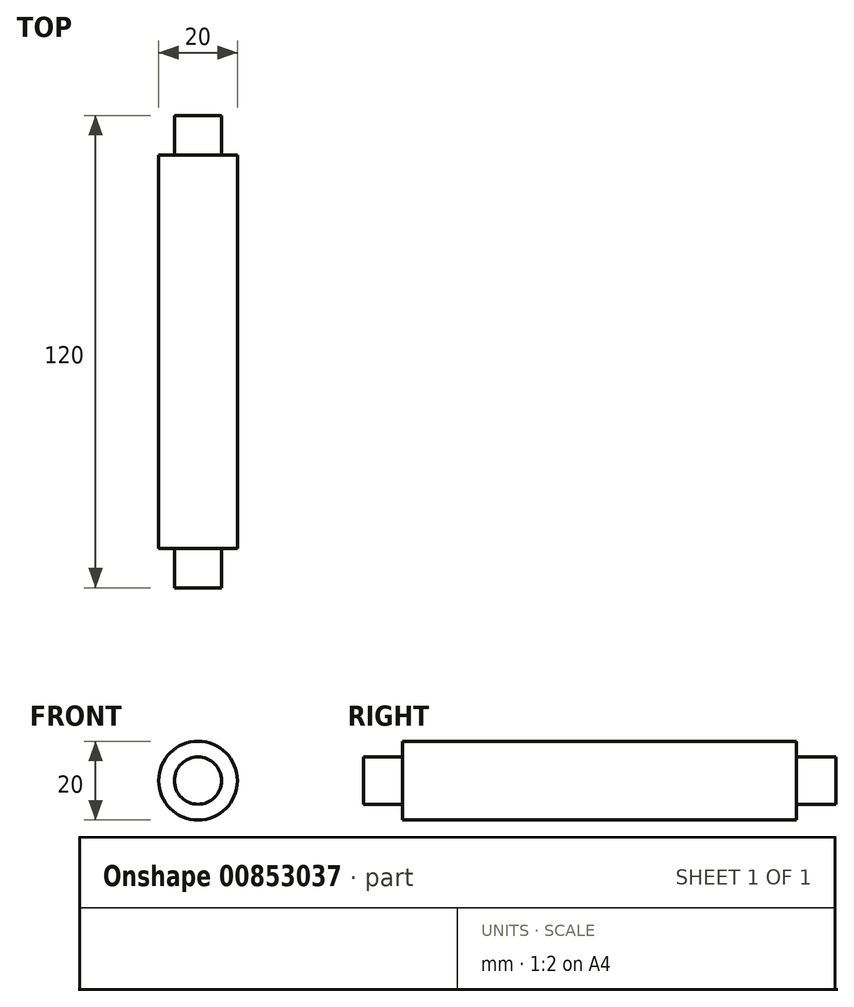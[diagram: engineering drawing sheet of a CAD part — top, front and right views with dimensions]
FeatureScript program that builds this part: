
annotation { "Feature Type Name" : "Feature", "Feature Type Description" : "" }
export const myFeature = defineFeature(function(context is Context, id is Id, definition is map)
    precondition{}
    {
        {
            var Q0;
            Q0=qCreatedBy(makeId("Top.planeOp"),FACE);
            var sketch = newSketch(context, id + "F0", { "sketchPlane" : qUnion([Q0])});
            skLineSegment(sketch, "E0.bottom", {"start": v(5.8, 50) * mm, "end": v(9.8, 50) * mm});
            skLineSegment(sketch, "E0.top", {"start": v(5.8, -50) * mm, "end": v(9.8, -50) * mm});
            skLineSegment(sketch, "E0.left", {"start": v(-0.2, 50) * mm, "end": v(-0.2, -50) * mm});
            skLineSegment(sketch, "E0.right", {"start": v(9.8, 50) * mm, "end": v(9.8, -50) * mm});
            skLineSegment(sketch, "E1.top", {"start": v(-0.2, 60) * mm, "end": v(5.8, 60) * mm});
            skLineSegment(sketch, "E1.left", {"start": v(-0.2, 50) * mm, "end": v(-0.2, 60) * mm});
            skLineSegment(sketch, "E1.right", {"start": v(5.8, 50) * mm, "end": v(5.8, 60) * mm});
            skLineSegment(sketch, "E2.top", {"start": v(-0.2, -60) * mm, "end": v(5.8, -60) * mm});
            skLineSegment(sketch, "E2.left", {"start": v(-0.2, -50) * mm, "end": v(-0.2, -60) * mm});
            skLineSegment(sketch, "E2.right", {"start": v(5.8, -50) * mm, "end": v(5.8, -60) * mm});
            skSolve(sketch);
        }
        {
            var Q0;
            Q0=makeQuery(id+"F0.imprint","IMPRINT",FACE,{"disambiguationData":[TD([[makeQuery(id+"F0.imprint","IMPRINT",EDGE,{"derivedFrom":sQuery(id+"F0.wireOp",EDGE,"E0.bottom")}),-1.0]])]});
            var Q1;
            Q1=sQuery(id+"F0.wireOp",EDGE,"E0.left");
            revolve(context, id + "F1", {"surfaceOperationType" : NewSurfaceOperationType.NEW, "entities" : qUnion([Q0]), "axis" : qUnion([Q1]), "revolveType" : RevolveType.FULL});
        }
    });
